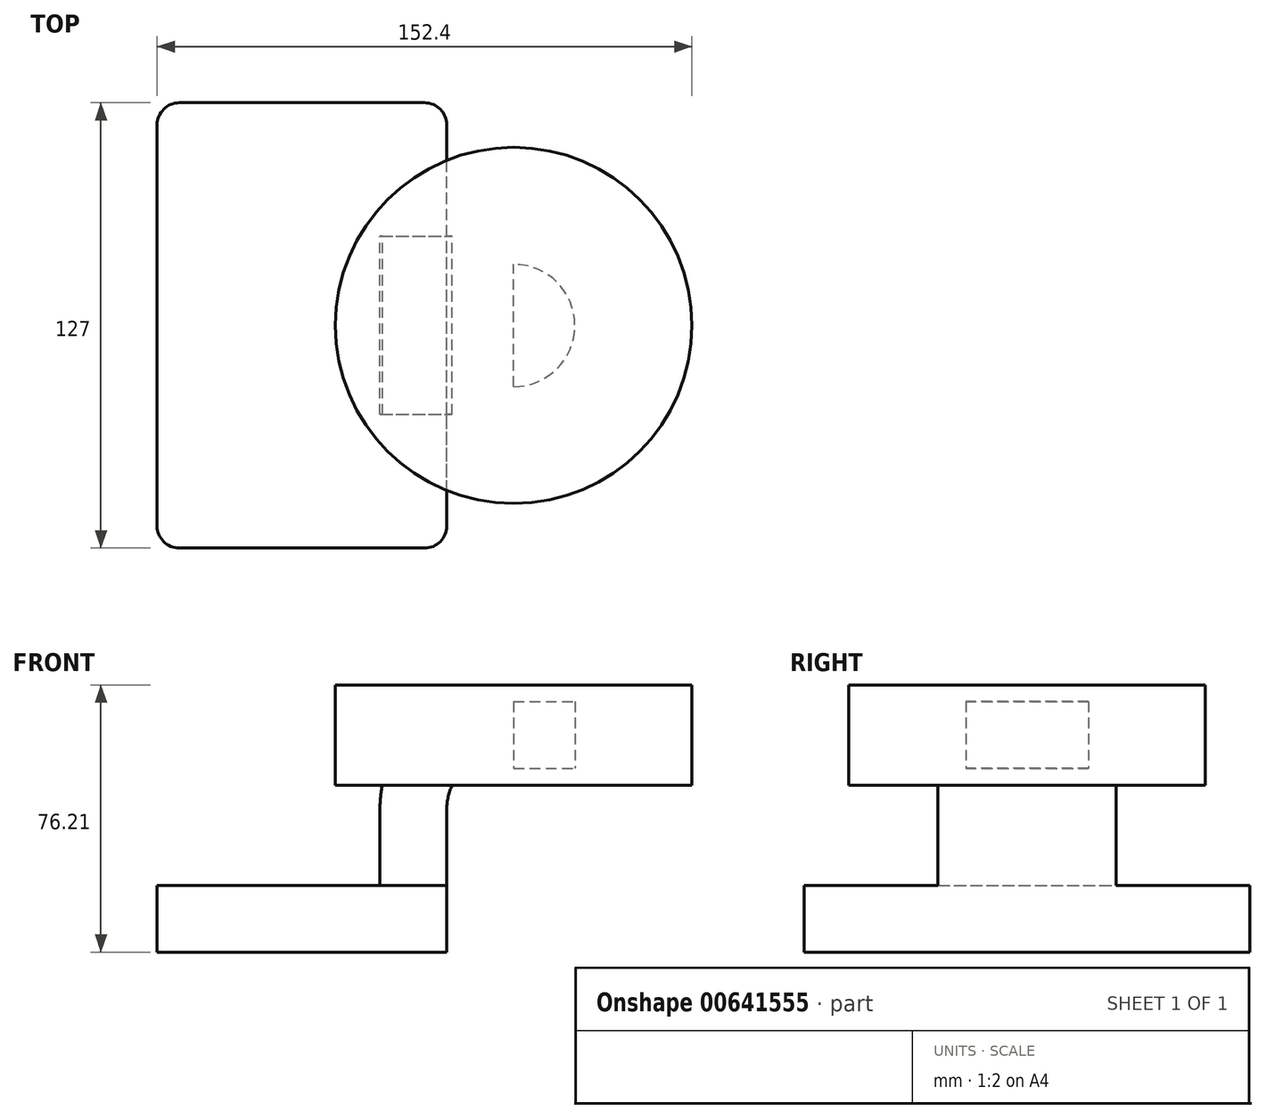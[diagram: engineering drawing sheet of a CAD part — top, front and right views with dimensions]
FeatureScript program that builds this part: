
annotation { "Feature Type Name" : "Feature", "Feature Type Description" : "" }
export const myFeature = defineFeature(function(context is Context, id is Id, definition is map)
    precondition{}
    {
        {
            var Q0;
            Q0=qCreatedBy(makeId("Front.planeOp"),FACE);
            var sketch = newSketch(context, id + "F0", { "sketchPlane" : qUnion([Q0])});
            skLineSegment(sketch, "E0.bottom", {"start": v(-41.28, -9.53) * mm, "end": v(41.28, -9.53) * mm});
            skLineSegment(sketch, "E0.top", {"start": v(-41.28, 9.52) * mm, "end": v(41.28, 9.52) * mm});
            skLineSegment(sketch, "E0.left", {"start": v(-41.28, -9.53) * mm, "end": v(-41.28, 9.53) * mm});
            skLineSegment(sketch, "E0.right", {"start": v(41.28, -9.53) * mm, "end": v(41.28, 9.52) * mm});
            skPoint(sketch, "E0.middle", {"position": v(0, 0) * mm});
            skLineSegment(sketch, "E1.bottom", {"start": v(60.32, 38.1) * mm, "end": v(111.12, 38.1) * mm});
            skLineSegment(sketch, "E1.top", {"start": v(60.32, 66.67) * mm, "end": v(111.12, 66.67) * mm});
            skLineSegment(sketch, "E1.left", {"start": v(60.32, 38.1) * mm, "end": v(60.32, 66.67) * mm});
            skLineSegment(sketch, "E1.right", {"start": v(111.12, 38.1) * mm, "end": v(111.12, 66.67) * mm});
            skPoint(sketch, "E1.middle", {"position": v(85.72, 52.39) * mm});
            skLineSegment(sketch, "E2", {"start": v(41.28, 9.52) * mm, "end": v(41.28, 31.26) * mm});
            skArc(sketch, "E3", {"start": v(41.27, 31.26) * mm, "mid": v(42.6, 37.6) * mm, "end": v(46.33, 42.88) * mm});
            skLineSegment(sketch, "E4", {"start": v(46.33, 42.88) * mm, "end": v(77.77, 42.88) * mm});
            skLineSegment(sketch, "E5.0", {"start": v(40.44, 61.93) * mm, "end": v(77.77, 61.93) * mm});
            skArc(sketch, "E5.1", {"start": v(22.23, 31.26) * mm, "mid": v(27.12, 49.1) * mm, "end": v(40.44, 61.93) * mm});
            skLineSegment(sketch, "E5.2", {"start": v(22.23, 9.52) * mm, "end": v(22.23, 31.26) * mm});
            skLineSegment(sketch, "E6", {"start": v(77.77, 42.88) * mm, "end": v(77.77, 61.93) * mm});
            skFitSpline(sketch, "E7", {"points": [v(-41.28, 9.53) * mm, v(40.44, 61.93) * mm], "startDerivative": vector(-0.88, 103.36) * mm, "endDerivative": vector(104.48, 2.69) * mm});
            skSolve(sketch);
        }
        {
            var Q0;
            Q0=makeQuery(id+"F0.imprint","IMPRINT",FACE,{"disambiguationData":[TD([[makeQuery(id+"F0.imprint","IMPRINT",EDGE,{"derivedFrom":sQuery(id+"F0.wireOp",EDGE,"E0.bottom")}),1.0]])]});
            extrude(context, id + "F1", {"entities" : qUnion([Q0]), "endBound" : BoundingType.SYMMETRIC, "depth" : 127 * mm, "offsetDistance" : 25.4 * mm});
        }
        {
            var Q0;
            {var subQ0=sQuery(id+"F0.wireOp",EDGE,"E2");Q0=makeQuery(id+"F0.imprint","IMPRINT",FACE,{"disambiguationData":[TD([[makeQuery(id+"F0.imprint","IMPRINT",EDGE,{"derivedFrom":subQ0}),1.0]])]});}
            extrude(context, id + "F2", {"entities" : qUnion([Q0]), "operationType" : NewBodyOperationType.ADD, "endBound" : BoundingType.SYMMETRIC, "depth" : 50.8 * mm, "offsetDistance" : 25.4 * mm});
        }
        {
            var Q0;
            Q0=makeQuery(id+"F0.imprint","IMPRINT",FACE,{"disambiguationData":[TD([[makeQuery(id+"F0.imprint","IMPRINT",EDGE,{"derivedFrom":sQuery(id+"F0.wireOp",EDGE,"E5.1")}),1.0]])]});
            extrude(context, id + "F3", {"entities" : qUnion([Q0]), "operationType" : NewBodyOperationType.ADD, "endBound" : BoundingType.SYMMETRIC, "oppositeDirection" : true, "depth" : 15.88 * mm, "offsetDistance" : 25.4 * mm});
        }
        {
            var Q0;
            {var subQ4=sQuery(id+"F0.wireOp",EDGE,"E1.bottom");Q0=makeQuery(id+"F0.imprint","IMPRINT",FACE,{"disambiguationData":[TD([[makeQuery(id+"F0.imprint","IMPRINT",EDGE,{"derivedFrom":subQ4}),1.0]])]});}
            var Q1;
            Q1=sQuery(id+"F0.wireOp",EDGE,"E1.left");
            revolve(context, id + "F4", {"operationType" : NewBodyOperationType.ADD, "entities" : qUnion([Q0]), "axis" : qUnion([Q1]), "revolveType" : RevolveType.FULL});
        }
        {
            var Q0;
            Q0=makeQuery(id+"F1.opExtrude","CAP_EDGE",EDGE,{"disambiguationData":[OSD([sQuery(id+"F0.wireOp",EDGE,"E0.left")])],"isStart":false});
            var Q1;
            Q1=makeQuery(id+"F1.opExtrude","CAP_EDGE",EDGE,{"disambiguationData":[OSD([sQuery(id+"F0.wireOp",EDGE,"E0.right")])],"isStart":false});
            var Q2;
            Q2=makeQuery(id+"F1.opExtrude","CAP_EDGE",EDGE,{"disambiguationData":[OSD([sQuery(id+"F0.wireOp",EDGE,"E0.right")])],"isStart":true});
            var Q3;
            Q3=makeQuery(id+"F1.opExtrude","CAP_EDGE",EDGE,{"disambiguationData":[OSD([sQuery(id+"F0.wireOp",EDGE,"E0.left")])],"isStart":true});
            fillet(context, id + "F5", {"entities" : qUnion([Q0, Q1, Q2, Q3]), "radius" : 6.35 * mm, "tangentPropagation" : true, "allowEdgeOverflow" : false});
        }
    });
